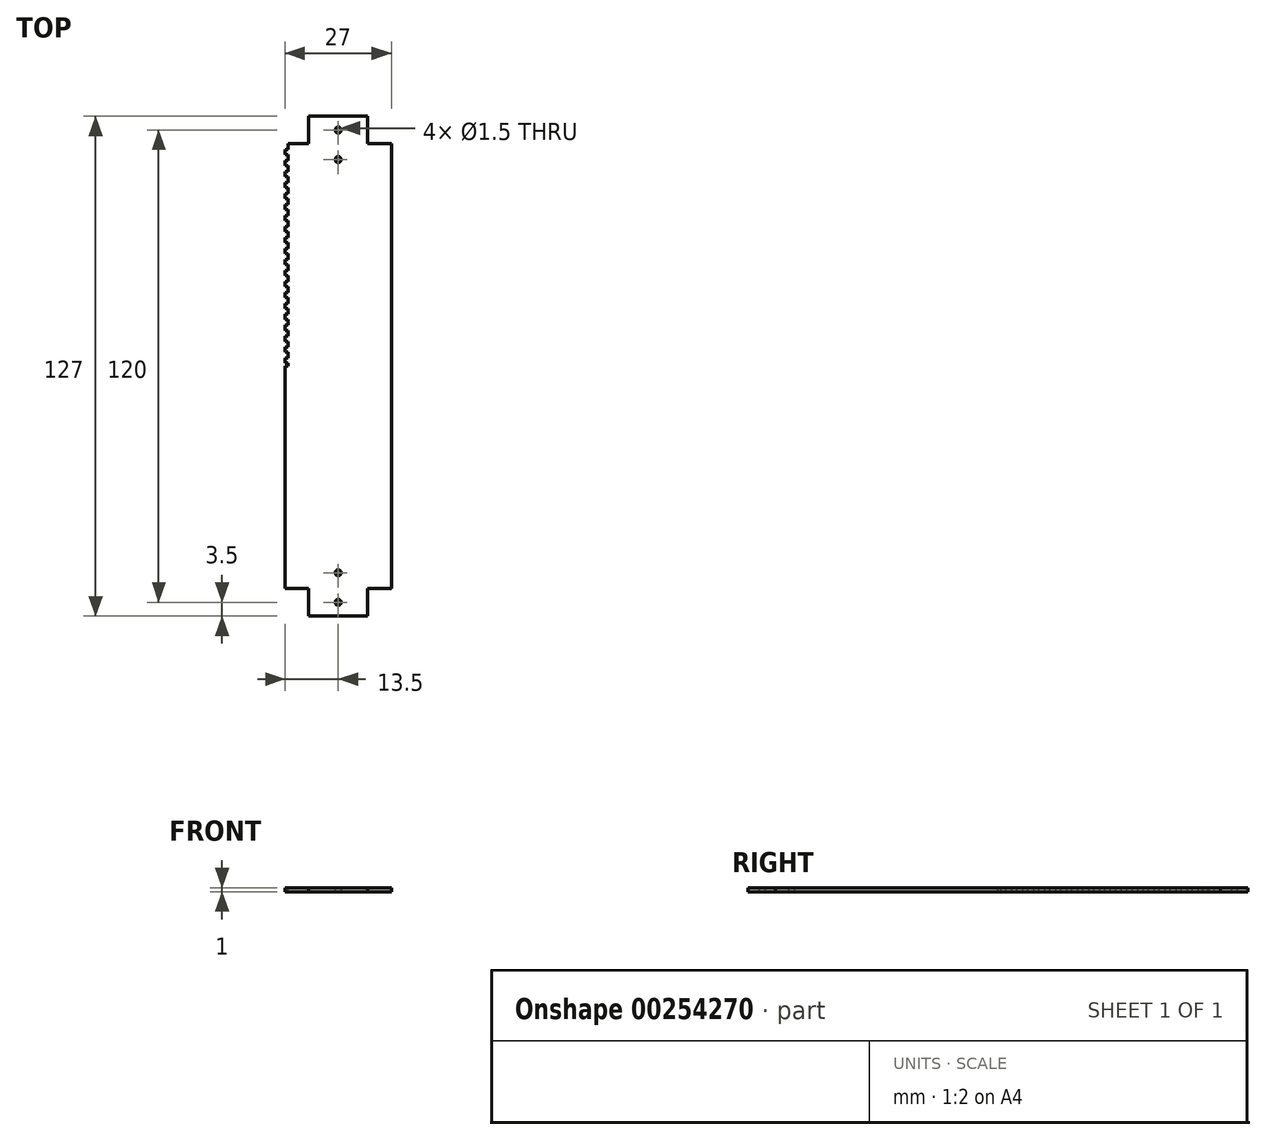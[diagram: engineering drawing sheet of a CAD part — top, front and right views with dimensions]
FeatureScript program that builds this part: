
annotation { "Feature Type Name" : "Feature", "Feature Type Description" : "" }
export const myFeature = defineFeature(function(context is Context, id is Id, definition is map)
    precondition{}
    {
        {
            var Q0;
            Q0=qCreatedBy(makeId("Top.planeOp"),FACE);
            var sketch = newSketch(context, id + "F0", { "sketchPlane" : qUnion([Q0])});
            skLineSegment(sketch, "E0", {"start": v(-13.5, 0) * mm, "end": v(-13.5, 56.5) * mm});
            skLineSegment(sketch, "E1", {"start": v(-13.5, 56.5) * mm, "end": v(-7.5, 56.5) * mm});
            skLineSegment(sketch, "E2", {"start": v(-7.5, 56.5) * mm, "end": v(-7.5, 63.5) * mm});
            skLineSegment(sketch, "E3", {"start": v(-7.5, 63.5) * mm, "end": v(0, 63.5) * mm});
            skLineSegment(sketch, "E4", {"start": v(-13.5, 0) * mm, "end": v(0, 0) * mm});
            skLineSegment(sketch, "E5", {"start": v(0, 0) * mm, "end": v(0, 63.5) * mm});
            skPoint(sketch, "E6", {"position": v(-7.5, 60) * mm});
            skCircle(sketch, "E7", {"center": v(0, 60) * mm, "radius": 0.75 * mm});
            skCircle(sketch, "E8", {"center": v(0, 52.5) * mm, "radius": 0.75 * mm});
            skSolve(sketch);
        }
        {
            var Q0;
            Q0=makeQuery(id+"F0.imprint","IMPRINT",FACE,{"disambiguationData":[TD([[makeQuery(id+"F0.imprint","IMPRINT",EDGE,{"derivedFrom":sQuery(id+"F0.wireOp",EDGE,"E0")}),-1.0]])]});
            extrude(context, id + "F1", {"entities" : qUnion([Q0]), "depth" : 1 * mm, "offsetDistance" : 25 * mm});
        }
        {
            var Q0;
            Q0=makeQuery(id+"F1.opExtrude","SWEPT_BODY",BODY,{"disambiguationData":[OSD([sQuery(id+"F0.wireOp",EDGE,"E0"),sQuery(id+"F0.wireOp",EDGE,"E1"),sQuery(id+"F0.wireOp",EDGE,"E2"),sQuery(id+"F0.wireOp",EDGE,"E3"),sQuery(id+"F0.wireOp",EDGE,"E4"),sQuery(id+"F0.wireOp",EDGE,"E5"),sQuery(id+"F0.wireOp",EDGE,"E7")])]});
            var Q1;
            {var subQ0=sQuery(id+"F0.wireOp",EDGE,"E5");Q1=makeQuery(id+"F1.opExtrude","SWEPT_FACE",FACE,{"disambiguationData":[OSD([subQ0]),TDD([makeQuery(id+"F0.imprint","IMPRINT",EDGE,{"disambiguationData":[TD([[makeQuery(id+"F0.imprint","INTERSECT",VERTEX,{"derivedFrom":[sQuery(id+"F0.wireOp",EDGE,"E4"),subQ0]}),-1.0]])],"derivedFrom":subQ0})])]});}
            mirror(context, id + "F2", {"operationType" : NewBodyOperationType.ADD, "entities" : qUnion([Q0]), "mirrorPlane" : qUnion([Q1])});
        }
        {
            var Q0;
            Q0=makeQuery(id+"F1.opExtrude","SWEPT_BODY",BODY,{"disambiguationData":[OSD([sQuery(id+"F0.wireOp",EDGE,"E0"),sQuery(id+"F0.wireOp",EDGE,"E1"),sQuery(id+"F0.wireOp",EDGE,"E2"),sQuery(id+"F0.wireOp",EDGE,"E3"),sQuery(id+"F0.wireOp",EDGE,"E4"),sQuery(id+"F0.wireOp",EDGE,"E5"),sQuery(id+"F0.wireOp",EDGE,"E7")])]});
            var Q1;
            {var subQ0=makeQuery(id+"F1.opExtrude","SWEPT_FACE",FACE,{"disambiguationData":[OSD([sQuery(id+"F0.wireOp",EDGE,"E4")])]});Q1=makeQuery(id+"F2.boolean.opBoolean","MERGE",FACE,{"derivedFrom":[subQ0,makeQuery(id+"F2.opPattern","COPY",FACE,{"derivedFrom":subQ0,"instanceName":"1"})]});}
            mirror(context, id + "F3", {"operationType" : NewBodyOperationType.ADD, "entities" : qUnion([Q0]), "mirrorPlane" : qUnion([Q1])});
        }
        {
            var Q0;
            {var subQ0=makeQuery(id+"F1.opExtrude","CAP_FACE",FACE,{"disambiguationData":[OSD([sQuery(id+"F0.wireOp",EDGE,"E0"),sQuery(id+"F0.wireOp",EDGE,"E1"),sQuery(id+"F0.wireOp",EDGE,"E2"),sQuery(id+"F0.wireOp",EDGE,"E3"),sQuery(id+"F0.wireOp",EDGE,"E4"),sQuery(id+"F0.wireOp",EDGE,"E5"),sQuery(id+"F0.wireOp",EDGE,"E7"),sQuery(id+"F0.wireOp",EDGE,"E8")])],"isStart":false});var subQ1=makeQuery(id+"F2.boolean.opBoolean","MERGE",FACE,{"derivedFrom":[subQ0,makeQuery(id+"F2.opPattern","COPY",FACE,{"derivedFrom":subQ0,"instanceName":"1"})]});Q0=makeQuery(id+"F3.boolean.opBoolean","MERGE",FACE,{"derivedFrom":[subQ1,makeQuery(id+"F3.opPattern","COPY",FACE,{"derivedFrom":subQ1,"instanceName":"1"})]});}
            var sketch = newSketch(context, id + "F4", { "sketchPlane" : qUnion([Q0])});
            skLineSegment(sketch, "E9.0", {"start": v(13.5, -56.5) * mm, "end": v(13.5, 56.5) * mm, "construction": true});
            skLineSegment(sketch, "E10", {"start": v(-12.75, 55.75) * mm, "end": v(-12.75, 55) * mm});
            skLineSegment(sketch, "E11", {"start": v(-12.75, 55) * mm, "end": v(-13.5, 55) * mm});
            skLineSegment(sketch, "E12", {"start": v(-13.5, 55) * mm, "end": v(-13.5, 53.71) * mm});
            skLineSegment(sketch, "E13", {"start": v(-13.5, 53.71) * mm, "end": v(-12.75, 53.71) * mm});
            skLineSegment(sketch, "E14", {"start": v(-12.75, 53.71) * mm, "end": v(-12.75, 52.96) * mm});
            skLineSegment(sketch, "E15", {"start": v(-12.75, 55.75) * mm, "end": v(-12.75, 56.5) * mm});
            skLineSegment(sketch, "E16", {"start": v(-12.75, 55) * mm, "end": v(-12, 55) * mm, "construction": true});
            skLineSegment(sketch, "E17", {"start": v(-12, 55) * mm, "end": v(-12, 56.5) * mm, "construction": true});
            skPoint(sketch, "E18", {"position": v(-13.5, 0) * mm});
            skLineSegment(sketch, "E19.0.1.0", {"start": v(-12.75, 52.96) * mm, "end": v(-12.75, 52.21) * mm});
            skLineSegment(sketch, "E19.0.1.1", {"start": v(-12.75, 52.21) * mm, "end": v(-13.5, 52.21) * mm});
            skLineSegment(sketch, "E19.0.1.2", {"start": v(-13.5, 52.21) * mm, "end": v(-13.5, 50.93) * mm});
            skLineSegment(sketch, "E19.0.1.3", {"start": v(-13.5, 50.93) * mm, "end": v(-12.75, 50.93) * mm});
            skLineSegment(sketch, "E19.0.1.4", {"start": v(-12.75, 50.93) * mm, "end": v(-12.75, 50.18) * mm});
            skLineSegment(sketch, "E19.0.2.0", {"start": v(-12.75, 50.17) * mm, "end": v(-12.75, 49.42) * mm});
            skLineSegment(sketch, "E19.0.2.1", {"start": v(-12.75, 49.42) * mm, "end": v(-13.5, 49.42) * mm});
            skLineSegment(sketch, "E19.0.2.2", {"start": v(-13.5, 49.42) * mm, "end": v(-13.5, 48.14) * mm});
            skLineSegment(sketch, "E19.0.2.3", {"start": v(-13.5, 48.14) * mm, "end": v(-12.75, 48.14) * mm});
            skLineSegment(sketch, "E19.0.2.4", {"start": v(-12.75, 48.14) * mm, "end": v(-12.75, 47.39) * mm});
            skLineSegment(sketch, "E19.direction1", {"start": v(-12.75, 55) * mm, "end": v(-12.75, 55) * mm});
            skLineSegment(sketch, "E19.direction2", {"start": v(-12.75, 55) * mm, "end": v(-12.75, 52.21) * mm, "construction": true});
            skLineSegment(sketch, "E20.0.0.3", {"start": v(-12.75, 47.39) * mm, "end": v(-12.75, 46.64) * mm});
            skLineSegment(sketch, "E20.3.0.3", {"start": v(-12.75, 46.64) * mm, "end": v(-13.5, 46.64) * mm});
            skLineSegment(sketch, "E20.6.0.3", {"start": v(-13.5, 46.64) * mm, "end": v(-13.5, 45.35) * mm});
            skLineSegment(sketch, "E20.9.0.3", {"start": v(-13.5, 45.35) * mm, "end": v(-12.75, 45.35) * mm});
            skLineSegment(sketch, "E20.12.0.3", {"start": v(-12.75, 45.35) * mm, "end": v(-12.75, 44.6) * mm});
            skLineSegment(sketch, "E20.0.0.4", {"start": v(-12.75, 44.6) * mm, "end": v(-12.75, 43.85) * mm});
            skLineSegment(sketch, "E20.3.0.4", {"start": v(-12.75, 43.85) * mm, "end": v(-13.5, 43.85) * mm});
            skLineSegment(sketch, "E20.6.0.4", {"start": v(-13.5, 43.85) * mm, "end": v(-13.5, 42.56) * mm});
            skLineSegment(sketch, "E20.9.0.4", {"start": v(-13.5, 42.56) * mm, "end": v(-12.75, 42.56) * mm});
            skLineSegment(sketch, "E20.12.0.4", {"start": v(-12.75, 42.56) * mm, "end": v(-12.75, 41.81) * mm});
            skLineSegment(sketch, "E20.0.0.5", {"start": v(-12.75, 41.81) * mm, "end": v(-12.75, 41.06) * mm});
            skLineSegment(sketch, "E20.3.0.5", {"start": v(-12.75, 41.06) * mm, "end": v(-13.5, 41.06) * mm});
            skLineSegment(sketch, "E20.6.0.5", {"start": v(-13.5, 41.06) * mm, "end": v(-13.5, 39.78) * mm});
            skLineSegment(sketch, "E20.9.0.5", {"start": v(-13.5, 39.78) * mm, "end": v(-12.75, 39.78) * mm});
            skLineSegment(sketch, "E20.12.0.5", {"start": v(-12.75, 39.78) * mm, "end": v(-12.75, 39.03) * mm});
            skLineSegment(sketch, "E20.0.0.6", {"start": v(-12.75, 39.03) * mm, "end": v(-12.75, 38.28) * mm});
            skLineSegment(sketch, "E20.3.0.6", {"start": v(-12.75, 38.28) * mm, "end": v(-13.5, 38.28) * mm});
            skLineSegment(sketch, "E20.6.0.6", {"start": v(-13.5, 38.28) * mm, "end": v(-13.5, 36.99) * mm});
            skLineSegment(sketch, "E20.9.0.6", {"start": v(-13.5, 36.99) * mm, "end": v(-12.75, 36.99) * mm});
            skLineSegment(sketch, "E20.12.0.6", {"start": v(-12.75, 36.99) * mm, "end": v(-12.75, 36.24) * mm});
            skLineSegment(sketch, "E20.0.0.7", {"start": v(-12.75, 36.24) * mm, "end": v(-12.75, 35.49) * mm});
            skLineSegment(sketch, "E20.3.0.7", {"start": v(-12.75, 35.49) * mm, "end": v(-13.5, 35.49) * mm});
            skLineSegment(sketch, "E20.6.0.7", {"start": v(-13.5, 35.49) * mm, "end": v(-13.5, 34.2) * mm});
            skLineSegment(sketch, "E20.9.0.7", {"start": v(-13.5, 34.2) * mm, "end": v(-12.75, 34.2) * mm});
            skLineSegment(sketch, "E20.12.0.7", {"start": v(-12.75, 34.2) * mm, "end": v(-12.75, 33.45) * mm});
            skLineSegment(sketch, "E20.0.0.8", {"start": v(-12.75, 33.45) * mm, "end": v(-12.75, 32.7) * mm});
            skLineSegment(sketch, "E20.3.0.8", {"start": v(-12.75, 32.7) * mm, "end": v(-13.5, 32.7) * mm});
            skLineSegment(sketch, "E20.6.0.8", {"start": v(-13.5, 32.7) * mm, "end": v(-13.5, 31.41) * mm});
            skLineSegment(sketch, "E20.9.0.8", {"start": v(-13.5, 31.41) * mm, "end": v(-12.75, 31.41) * mm});
            skLineSegment(sketch, "E20.12.0.8", {"start": v(-12.75, 31.41) * mm, "end": v(-12.75, 30.66) * mm});
            skLineSegment(sketch, "E20.0.0.9", {"start": v(-12.75, 30.66) * mm, "end": v(-12.75, 29.91) * mm});
            skLineSegment(sketch, "E20.3.0.9", {"start": v(-12.75, 29.91) * mm, "end": v(-13.5, 29.91) * mm});
            skLineSegment(sketch, "E20.6.0.9", {"start": v(-13.5, 29.91) * mm, "end": v(-13.5, 28.63) * mm});
            skLineSegment(sketch, "E20.9.0.9", {"start": v(-13.5, 28.63) * mm, "end": v(-12.75, 28.63) * mm});
            skLineSegment(sketch, "E20.12.0.9", {"start": v(-12.75, 28.63) * mm, "end": v(-12.75, 27.88) * mm});
            skLineSegment(sketch, "E20.0.0.10", {"start": v(-12.75, 27.88) * mm, "end": v(-12.75, 27.12) * mm});
            skLineSegment(sketch, "E20.3.0.10", {"start": v(-12.75, 27.12) * mm, "end": v(-13.5, 27.12) * mm});
            skLineSegment(sketch, "E20.6.0.10", {"start": v(-13.5, 27.12) * mm, "end": v(-13.5, 25.84) * mm});
            skLineSegment(sketch, "E20.9.0.10", {"start": v(-13.5, 25.84) * mm, "end": v(-12.75, 25.84) * mm});
            skLineSegment(sketch, "E20.12.0.10", {"start": v(-12.75, 25.84) * mm, "end": v(-12.75, 25.09) * mm});
            skLineSegment(sketch, "E20.0.0.11", {"start": v(-12.75, 25.09) * mm, "end": v(-12.75, 24.34) * mm});
            skLineSegment(sketch, "E20.3.0.11", {"start": v(-12.75, 24.34) * mm, "end": v(-13.5, 24.34) * mm});
            skLineSegment(sketch, "E20.6.0.11", {"start": v(-13.5, 24.34) * mm, "end": v(-13.5, 23.05) * mm});
            skLineSegment(sketch, "E20.9.0.11", {"start": v(-13.5, 23.05) * mm, "end": v(-12.75, 23.05) * mm});
            skLineSegment(sketch, "E20.12.0.11", {"start": v(-12.75, 23.05) * mm, "end": v(-12.75, 22.3) * mm});
            skLineSegment(sketch, "E20.0.0.12", {"start": v(-12.75, 22.3) * mm, "end": v(-12.75, 21.55) * mm});
            skLineSegment(sketch, "E20.3.0.12", {"start": v(-12.75, 21.55) * mm, "end": v(-13.5, 21.55) * mm});
            skLineSegment(sketch, "E20.6.0.12", {"start": v(-13.5, 21.55) * mm, "end": v(-13.5, 20.26) * mm});
            skLineSegment(sketch, "E20.9.0.12", {"start": v(-13.5, 20.26) * mm, "end": v(-12.75, 20.26) * mm});
            skLineSegment(sketch, "E20.12.0.12", {"start": v(-12.75, 20.26) * mm, "end": v(-12.75, 19.51) * mm});
            skLineSegment(sketch, "E20.0.0.13", {"start": v(-12.75, 19.51) * mm, "end": v(-12.75, 18.76) * mm});
            skLineSegment(sketch, "E20.3.0.13", {"start": v(-12.75, 18.76) * mm, "end": v(-13.5, 18.76) * mm});
            skLineSegment(sketch, "E20.6.0.13", {"start": v(-13.5, 18.76) * mm, "end": v(-13.5, 17.48) * mm});
            skLineSegment(sketch, "E20.9.0.13", {"start": v(-13.5, 17.48) * mm, "end": v(-12.75, 17.48) * mm});
            skLineSegment(sketch, "E20.12.0.13", {"start": v(-12.75, 17.48) * mm, "end": v(-12.75, 16.73) * mm});
            skLineSegment(sketch, "E20.0.0.14", {"start": v(-12.75, 16.72) * mm, "end": v(-12.75, 15.97) * mm});
            skLineSegment(sketch, "E20.3.0.14", {"start": v(-12.75, 15.97) * mm, "end": v(-13.5, 15.97) * mm});
            skLineSegment(sketch, "E20.6.0.14", {"start": v(-13.5, 15.97) * mm, "end": v(-13.5, 14.69) * mm});
            skLineSegment(sketch, "E20.9.0.14", {"start": v(-13.5, 14.69) * mm, "end": v(-12.75, 14.69) * mm});
            skLineSegment(sketch, "E20.12.0.14", {"start": v(-12.75, 14.69) * mm, "end": v(-12.75, 13.94) * mm});
            skLineSegment(sketch, "E20.0.0.15", {"start": v(-12.75, 13.94) * mm, "end": v(-12.75, 13.19) * mm});
            skLineSegment(sketch, "E20.3.0.15", {"start": v(-12.75, 13.19) * mm, "end": v(-13.5, 13.19) * mm});
            skLineSegment(sketch, "E20.6.0.15", {"start": v(-13.5, 13.19) * mm, "end": v(-13.5, 11.9) * mm});
            skLineSegment(sketch, "E20.9.0.15", {"start": v(-13.5, 11.9) * mm, "end": v(-12.75, 11.9) * mm});
            skLineSegment(sketch, "E20.12.0.15", {"start": v(-12.75, 11.9) * mm, "end": v(-12.75, 11.15) * mm});
            skLineSegment(sketch, "E20.0.0.16", {"start": v(-12.75, 11.15) * mm, "end": v(-12.75, 10.4) * mm});
            skLineSegment(sketch, "E20.3.0.16", {"start": v(-12.75, 10.4) * mm, "end": v(-13.5, 10.4) * mm});
            skLineSegment(sketch, "E20.6.0.16", {"start": v(-13.5, 10.4) * mm, "end": v(-13.5, 9.11) * mm});
            skLineSegment(sketch, "E20.9.0.16", {"start": v(-13.5, 9.11) * mm, "end": v(-12.75, 9.11) * mm});
            skLineSegment(sketch, "E20.12.0.16", {"start": v(-12.75, 9.11) * mm, "end": v(-12.75, 8.36) * mm});
            skLineSegment(sketch, "E20.0.0.17", {"start": v(-12.75, 8.36) * mm, "end": v(-12.75, 7.61) * mm});
            skLineSegment(sketch, "E20.3.0.17", {"start": v(-12.75, 7.61) * mm, "end": v(-13.5, 7.61) * mm});
            skLineSegment(sketch, "E20.6.0.17", {"start": v(-13.5, 7.61) * mm, "end": v(-13.5, 6.33) * mm});
            skLineSegment(sketch, "E20.9.0.17", {"start": v(-13.5, 6.33) * mm, "end": v(-12.75, 6.33) * mm});
            skLineSegment(sketch, "E20.12.0.17", {"start": v(-12.75, 6.33) * mm, "end": v(-12.75, 5.58) * mm});
            skLineSegment(sketch, "E20.0.0.18", {"start": v(-12.75, 5.58) * mm, "end": v(-12.75, 4.83) * mm});
            skLineSegment(sketch, "E20.3.0.18", {"start": v(-12.75, 4.83) * mm, "end": v(-13.5, 4.83) * mm});
            skLineSegment(sketch, "E20.6.0.18", {"start": v(-13.5, 4.83) * mm, "end": v(-13.5, 3.54) * mm});
            skLineSegment(sketch, "E20.9.0.18", {"start": v(-13.5, 3.54) * mm, "end": v(-12.75, 3.54) * mm});
            skLineSegment(sketch, "E20.12.0.18", {"start": v(-12.75, 3.54) * mm, "end": v(-12.75, 2.79) * mm});
            skLineSegment(sketch, "E20.0.0.19", {"start": v(-12.75, 2.79) * mm, "end": v(-12.75, 2.04) * mm});
            skLineSegment(sketch, "E20.3.0.19", {"start": v(-12.75, 2.04) * mm, "end": v(-13.5, 2.04) * mm});
            skLineSegment(sketch, "E20.6.0.19", {"start": v(-13.5, 2.04) * mm, "end": v(-13.5, 0.75) * mm});
            skLineSegment(sketch, "E20.9.0.19", {"start": v(-13.5, 0.75) * mm, "end": v(-12.75, 0.75) * mm});
            skLineSegment(sketch, "E20.12.0.19", {"start": v(-12.75, 0.75) * mm, "end": v(-12.75, 0) * mm});
            skLineSegment(sketch, "E21", {"start": v(-12.75, 56.5) * mm, "end": v(-14.5, 56.5) * mm});
            skLineSegment(sketch, "E22", {"start": v(-14.5, 56.5) * mm, "end": v(-14.5, 0) * mm});
            skLineSegment(sketch, "E23", {"start": v(-14.5, 0) * mm, "end": v(-12.75, 0) * mm});
            skPoint(sketch, "E24", {"position": v(0, 63.5) * mm});
            skLineSegment(sketch, "E25", {"start": v(0, 63.5) * mm, "end": v(0, 52.5) * mm, "construction": true});
            skSolve(sketch);
        }
        {
            var Q0;
            {var subQ22=sQuery(id+"F4.wireOp",EDGE,"E12");Q0=makeQuery(id+"F4.imprint","IMPRINT",FACE,{"disambiguationData":[TD([[makeQuery(id+"F4.imprint","IMPRINT",EDGE,{"derivedFrom":subQ22}),1.0]])]});}
            var Q1;
            {var subQ1=sQuery(id+"F4.wireOp",EDGE,"E19.0.1.3");Q1=makeQuery(id+"F4.imprint","IMPRINT",FACE,{"disambiguationData":[TD([[makeQuery(id+"F4.imprint","IMPRINT",EDGE,{"derivedFrom":subQ1}),-1.0]])]});}
            var Q2;
            Q2=makeQuery(id+"F4.imprint","IMPRINT",FACE,{"disambiguationData":[TD([[makeQuery(id+"F4.imprint","IMPRINT",EDGE,{"derivedFrom":sQuery(id+"F4.wireOp",EDGE,"E10")}),-1.0]])]});
            var Q3;
            {var subQ1=sQuery(id+"F4.wireOp",EDGE,"E13");Q3=makeQuery(id+"F4.imprint","IMPRINT",FACE,{"disambiguationData":[TD([[makeQuery(id+"F4.imprint","IMPRINT",EDGE,{"derivedFrom":subQ1}),-1.0]])]});}
            var Q4;
            {var subQ1=sQuery(id+"F4.wireOp",EDGE,"E19.0.2.3");Q4=makeQuery(id+"F4.imprint","IMPRINT",FACE,{"disambiguationData":[TD([[makeQuery(id+"F4.imprint","IMPRINT",EDGE,{"derivedFrom":subQ1}),-1.0]])]});}
            var Q5;
            {var subQ1=sQuery(id+"F4.wireOp",EDGE,"E20.9.0.3");Q5=makeQuery(id+"F4.imprint","IMPRINT",FACE,{"disambiguationData":[TD([[makeQuery(id+"F4.imprint","IMPRINT",EDGE,{"derivedFrom":subQ1}),-1.0]])]});}
            var Q6;
            {var subQ1=sQuery(id+"F4.wireOp",EDGE,"E20.9.0.4");Q6=makeQuery(id+"F4.imprint","IMPRINT",FACE,{"disambiguationData":[TD([[makeQuery(id+"F4.imprint","IMPRINT",EDGE,{"derivedFrom":subQ1}),-1.0]])]});}
            var Q7;
            {var subQ1=sQuery(id+"F4.wireOp",EDGE,"E20.9.0.5");Q7=makeQuery(id+"F4.imprint","IMPRINT",FACE,{"disambiguationData":[TD([[makeQuery(id+"F4.imprint","IMPRINT",EDGE,{"derivedFrom":subQ1}),-1.0]])]});}
            var Q8;
            {var subQ1=sQuery(id+"F4.wireOp",EDGE,"E20.9.0.6");Q8=makeQuery(id+"F4.imprint","IMPRINT",FACE,{"disambiguationData":[TD([[makeQuery(id+"F4.imprint","IMPRINT",EDGE,{"derivedFrom":subQ1}),-1.0]])]});}
            var Q9;
            {var subQ1=sQuery(id+"F4.wireOp",EDGE,"E20.9.0.7");Q9=makeQuery(id+"F4.imprint","IMPRINT",FACE,{"disambiguationData":[TD([[makeQuery(id+"F4.imprint","IMPRINT",EDGE,{"derivedFrom":subQ1}),-1.0]])]});}
            var Q10;
            {var subQ1=sQuery(id+"F4.wireOp",EDGE,"E20.9.0.8");Q10=makeQuery(id+"F4.imprint","IMPRINT",FACE,{"disambiguationData":[TD([[makeQuery(id+"F4.imprint","IMPRINT",EDGE,{"derivedFrom":subQ1}),-1.0]])]});}
            var Q11;
            {var subQ1=sQuery(id+"F4.wireOp",EDGE,"E20.9.0.9");Q11=makeQuery(id+"F4.imprint","IMPRINT",FACE,{"disambiguationData":[TD([[makeQuery(id+"F4.imprint","IMPRINT",EDGE,{"derivedFrom":subQ1}),-1.0]])]});}
            var Q12;
            {var subQ1=sQuery(id+"F4.wireOp",EDGE,"E20.9.0.10");Q12=makeQuery(id+"F4.imprint","IMPRINT",FACE,{"disambiguationData":[TD([[makeQuery(id+"F4.imprint","IMPRINT",EDGE,{"derivedFrom":subQ1}),-1.0]])]});}
            var Q13;
            {var subQ1=sQuery(id+"F4.wireOp",EDGE,"E20.9.0.11");Q13=makeQuery(id+"F4.imprint","IMPRINT",FACE,{"disambiguationData":[TD([[makeQuery(id+"F4.imprint","IMPRINT",EDGE,{"derivedFrom":subQ1}),-1.0]])]});}
            var Q14;
            {var subQ1=sQuery(id+"F4.wireOp",EDGE,"E20.9.0.12");Q14=makeQuery(id+"F4.imprint","IMPRINT",FACE,{"disambiguationData":[TD([[makeQuery(id+"F4.imprint","IMPRINT",EDGE,{"derivedFrom":subQ1}),-1.0]])]});}
            var Q15;
            {var subQ1=sQuery(id+"F4.wireOp",EDGE,"E20.9.0.13");Q15=makeQuery(id+"F4.imprint","IMPRINT",FACE,{"disambiguationData":[TD([[makeQuery(id+"F4.imprint","IMPRINT",EDGE,{"derivedFrom":subQ1}),-1.0]])]});}
            var Q16;
            {var subQ1=sQuery(id+"F4.wireOp",EDGE,"E20.9.0.14");Q16=makeQuery(id+"F4.imprint","IMPRINT",FACE,{"disambiguationData":[TD([[makeQuery(id+"F4.imprint","IMPRINT",EDGE,{"derivedFrom":subQ1}),-1.0]])]});}
            var Q17;
            {var subQ1=sQuery(id+"F4.wireOp",EDGE,"E20.9.0.15");Q17=makeQuery(id+"F4.imprint","IMPRINT",FACE,{"disambiguationData":[TD([[makeQuery(id+"F4.imprint","IMPRINT",EDGE,{"derivedFrom":subQ1}),-1.0]])]});}
            var Q18;
            {var subQ1=sQuery(id+"F4.wireOp",EDGE,"E20.9.0.16");Q18=makeQuery(id+"F4.imprint","IMPRINT",FACE,{"disambiguationData":[TD([[makeQuery(id+"F4.imprint","IMPRINT",EDGE,{"derivedFrom":subQ1}),-1.0]])]});}
            var Q19;
            {var subQ1=sQuery(id+"F4.wireOp",EDGE,"E20.9.0.17");Q19=makeQuery(id+"F4.imprint","IMPRINT",FACE,{"disambiguationData":[TD([[makeQuery(id+"F4.imprint","IMPRINT",EDGE,{"derivedFrom":subQ1}),-1.0]])]});}
            var Q20;
            {var subQ1=sQuery(id+"F4.wireOp",EDGE,"E20.9.0.18");Q20=makeQuery(id+"F4.imprint","IMPRINT",FACE,{"disambiguationData":[TD([[makeQuery(id+"F4.imprint","IMPRINT",EDGE,{"derivedFrom":subQ1}),-1.0]])]});}
            var Q21;
            {var subQ0=sQuery(id+"F4.wireOp",EDGE,"E20.9.0.19");Q21=makeQuery(id+"F4.imprint","IMPRINT",FACE,{"disambiguationData":[TD([[makeQuery(id+"F4.imprint","IMPRINT",EDGE,{"derivedFrom":subQ0}),-1.0]])]});}
            var Q22;
            {var subQ0=makeQuery(id+"F1.opExtrude","CAP_FACE",FACE,{"disambiguationData":[OSD([sQuery(id+"F0.wireOp",EDGE,"E0"),sQuery(id+"F0.wireOp",EDGE,"E1"),sQuery(id+"F0.wireOp",EDGE,"E2"),sQuery(id+"F0.wireOp",EDGE,"E3"),sQuery(id+"F0.wireOp",EDGE,"E4"),sQuery(id+"F0.wireOp",EDGE,"E5"),sQuery(id+"F0.wireOp",EDGE,"E7"),sQuery(id+"F0.wireOp",EDGE,"E8")])],"isStart":true});var subQ1=makeQuery(id+"F2.boolean.opBoolean","MERGE",FACE,{"derivedFrom":[subQ0,makeQuery(id+"F2.opPattern","COPY",FACE,{"derivedFrom":subQ0,"instanceName":"1"})]});Q22=makeQuery(id+"F3.boolean.opBoolean","MERGE",FACE,{"derivedFrom":[subQ1,makeQuery(id+"F3.opPattern","COPY",FACE,{"derivedFrom":subQ1,"instanceName":"1"})]});}
            extrude(context, id + "F5", {"entities" : qUnion([Q0, Q1, Q2, Q3, Q4, Q5, Q6, Q7, Q8, Q9, Q10, Q11, Q12, Q13, Q14, Q15, Q16, Q17, Q18, Q19, Q20, Q21]), "operationType" : NewBodyOperationType.REMOVE, "endBound" : BoundingType.UP_TO_SURFACE, "oppositeDirection" : true, "depth" : 25 * mm, "endBoundEntityFace" : qUnion([Q22]), "offsetDistance" : 25 * mm});
        }
    });
